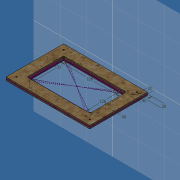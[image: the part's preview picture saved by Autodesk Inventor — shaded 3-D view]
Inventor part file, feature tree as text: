
AUTODESK INVENTOR PART (.ipt)
format: ipt  version: 2019 (Build 230136000, 136)  size: 150,016 bytes
history: native  units: mm
features: extrude x3, other x1, sketch x1
ambient origin geometry x8: Origin, YZ Plane, XZ Plane, XY Plane, X Axis, Y Axis, Z Axis, Center Point
bodies: Volumenkörper1 (feature_tree)
feature tree (5):
  other  "<userpath>\OneDrive\Dokumente\Inventor\Absauganlage\Absauganlage_Params.xlsx"
  sketch  "Skizze1"  dims[d0=140.0mm d1=240.0mm d2=5.0mm d3=232.0mm d4=132.0mm d5=2.0mm d6=128.0mm d7=228.0mm d8=2.0mm d10=6.0mm d14=6.0mm d15=0.0mm d16=6.0mm d17=0.0mm d19=40.0mm d20=40.0mm d21=5.5mm d23=20.0mm d24=20.0mm d25=10.0mm d26=0.0mm]
  extrude  "Extrusion1"  Depth=6.0mm
  extrude  "Extrusion2"  TaperAngle=0.0deg  [1 undecoded]
  extrude  "Extrusion3"  Depth=6.0mm
note: 1 required parameter value undecoded (feature->parameter linkage not recoverable at this tier; creation-order binding heuristic only, values carry confidence <= 0.55)
